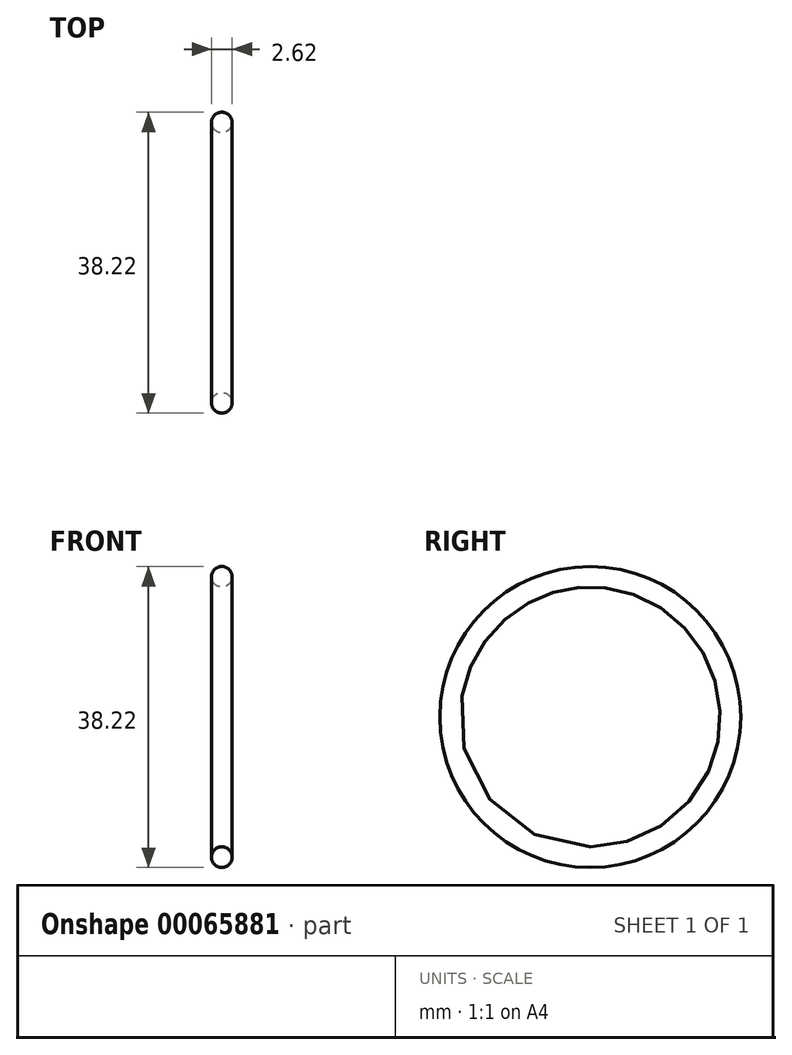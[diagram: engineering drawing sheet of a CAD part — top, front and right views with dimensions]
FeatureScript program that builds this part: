
annotation { "Feature Type Name" : "Feature", "Feature Type Description" : "" }
export const myFeature = defineFeature(function(context is Context, id is Id, definition is map)
    precondition{}
    {
        {
            var Q0;
            Q0=qCreatedBy(makeId("Front.planeOp"),FACE);
            var sketch = newSketch(context, id + "F0", { "sketchPlane" : qUnion([Q0])});
            skLineSegment(sketch, "E0", {"start": v(0, 0) * mm, "end": v(-6.06, 0) * mm, "construction": true});
            skCircle(sketch, "E1", {"center": v(0, 17.8) * mm, "radius": 1.3 * mm});
            skSolve(sketch);
        }
        {
            var Q0;
            Q0=makeQuery(id+"F0.imprint","IMPRINT",FACE,{"disambiguationData":[TD([[makeQuery(id+"F0.imprint","IMPRINT",EDGE,{"derivedFrom":sQuery(id+"F0.wireOp",EDGE,"E1")}),1.0]])]});
            var Q1;
            Q1=sQuery(id+"F0.wireOp",EDGE,"E0");
            revolve(context, id + "F1", {"entities" : qUnion([Q0]), "axis" : qUnion([Q1]), "revolveType" : RevolveType.FULL});
        }
    });
